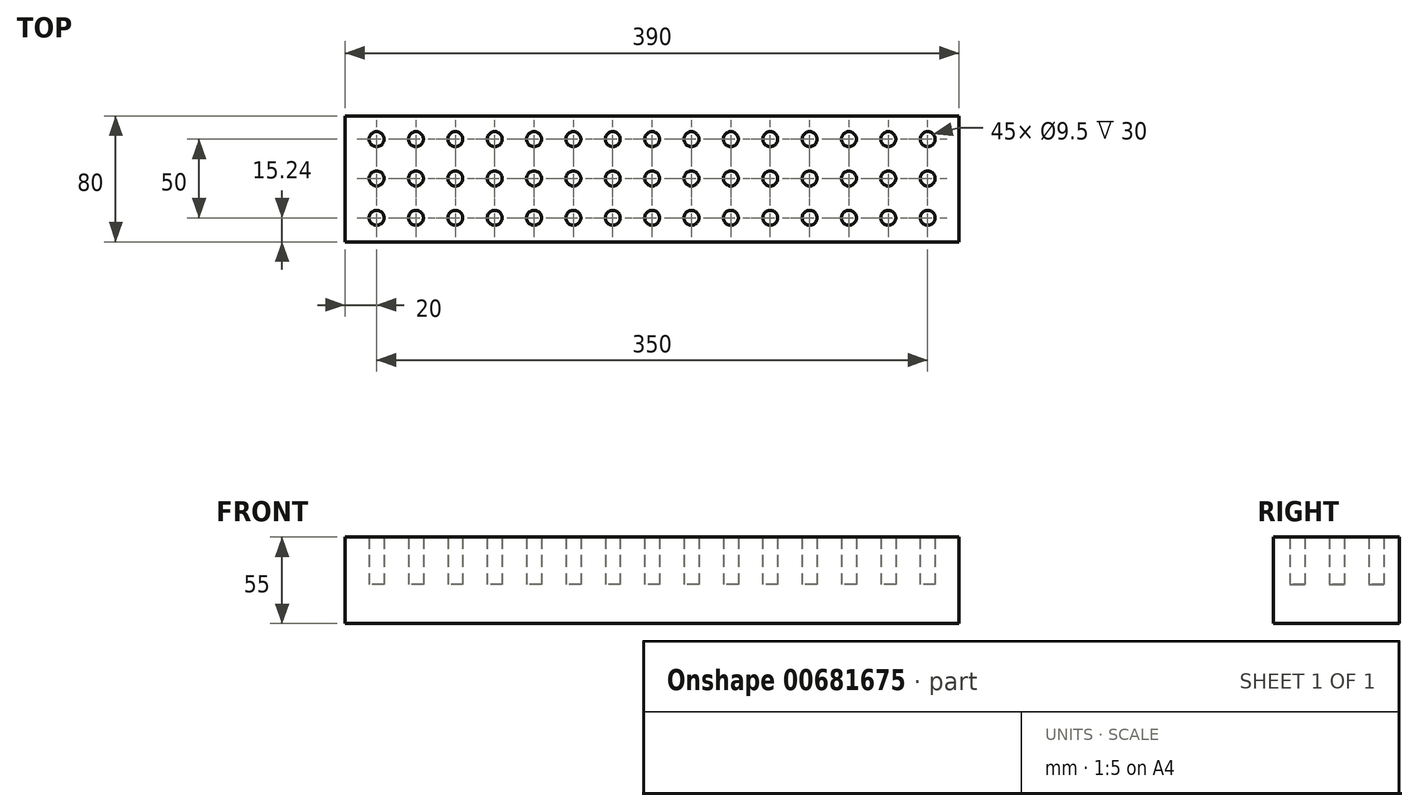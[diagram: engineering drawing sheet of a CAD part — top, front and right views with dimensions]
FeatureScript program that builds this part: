
annotation { "Feature Type Name" : "Feature", "Feature Type Description" : "" }
export const myFeature = defineFeature(function(context is Context, id is Id, definition is map)
    precondition{}
    {
        {
            var Q0;
            Q0=qCreatedBy(makeId("Top.planeOp"),FACE);
            var sketch = newSketch(context, id + "F0", { "sketchPlane" : qUnion([Q0])});
            skCircle(sketch, "E0.cCircle", {"center": v(0, 0) * mm, "radius": 4.11 * mm, "construction": true});
            skLineSegment(sketch, "E0.0", {"start": v(-0.03, 4.75) * mm, "end": v(4.1, 2.4) * mm});
            skLineSegment(sketch, "E0.1", {"start": v(4.1, 2.4) * mm, "end": v(4.13, -2.35) * mm});
            skLineSegment(sketch, "E0.2", {"start": v(4.13, -2.35) * mm, "end": v(0.03, -4.75) * mm});
            skLineSegment(sketch, "E0.3", {"start": v(0.03, -4.75) * mm, "end": v(-4.1, -2.4) * mm});
            skLineSegment(sketch, "E0.4", {"start": v(-4.1, -2.4) * mm, "end": v(-4.13, 2.35) * mm});
            skLineSegment(sketch, "E0.5", {"start": v(-4.13, 2.35) * mm, "end": v(-0.03, 4.75) * mm});
            skPoint(sketch, "E0.0.midPoint", {"position": v(2.04, 3.57) * mm});
            skCircle(sketch, "E1", {"center": v(0, 0) * mm, "radius": 4.75 * mm});
            skCircle(sketch, "E2.0.1.0", {"center": v(0, 25) * mm, "radius": 4.75 * mm});
            skCircle(sketch, "E2.0.2.0", {"center": v(0, 50) * mm, "radius": 4.75 * mm});
            skCircle(sketch, "E2.1.0.0", {"center": v(25, 0) * mm, "radius": 4.75 * mm});
            skCircle(sketch, "E2.1.1.0", {"center": v(25, 25) * mm, "radius": 4.75 * mm});
            skCircle(sketch, "E2.1.2.0", {"center": v(25, 50) * mm, "radius": 4.75 * mm});
            skCircle(sketch, "E2.2.0.0", {"center": v(50, 0) * mm, "radius": 4.75 * mm});
            skCircle(sketch, "E2.2.1.0", {"center": v(50, 25) * mm, "radius": 4.75 * mm});
            skCircle(sketch, "E2.2.2.0", {"center": v(50, 50) * mm, "radius": 4.75 * mm});
            skCircle(sketch, "E2.3.0.0", {"center": v(75, 0) * mm, "radius": 4.75 * mm});
            skCircle(sketch, "E2.3.1.0", {"center": v(75, 25) * mm, "radius": 4.75 * mm});
            skCircle(sketch, "E2.3.2.0", {"center": v(75, 50) * mm, "radius": 4.75 * mm});
            skCircle(sketch, "E2.4.0.0", {"center": v(100, 0) * mm, "radius": 4.75 * mm});
            skCircle(sketch, "E2.4.1.0", {"center": v(100, 25) * mm, "radius": 4.75 * mm});
            skCircle(sketch, "E2.4.2.0", {"center": v(100, 50) * mm, "radius": 4.75 * mm});
            skCircle(sketch, "E2.5.0.0", {"center": v(125, 0) * mm, "radius": 4.75 * mm});
            skCircle(sketch, "E2.5.1.0", {"center": v(125, 25) * mm, "radius": 4.75 * mm});
            skCircle(sketch, "E2.5.2.0", {"center": v(125, 50) * mm, "radius": 4.75 * mm});
            skCircle(sketch, "E2.6.0.0", {"center": v(150, 0) * mm, "radius": 4.75 * mm});
            skCircle(sketch, "E2.6.1.0", {"center": v(150, 25) * mm, "radius": 4.75 * mm});
            skCircle(sketch, "E2.6.2.0", {"center": v(150, 50) * mm, "radius": 4.75 * mm});
            skCircle(sketch, "E2.7.0.0", {"center": v(175, 0) * mm, "radius": 4.75 * mm});
            skCircle(sketch, "E2.7.1.0", {"center": v(175, 25) * mm, "radius": 4.75 * mm});
            skCircle(sketch, "E2.7.2.0", {"center": v(175, 50) * mm, "radius": 4.75 * mm});
            skCircle(sketch, "E2.8.0.0", {"center": v(200, 0) * mm, "radius": 4.75 * mm});
            skCircle(sketch, "E2.8.1.0", {"center": v(200, 25) * mm, "radius": 4.75 * mm});
            skCircle(sketch, "E2.8.2.0", {"center": v(200, 50) * mm, "radius": 4.75 * mm});
            skCircle(sketch, "E2.9.0.0", {"center": v(225, 0) * mm, "radius": 4.75 * mm});
            skCircle(sketch, "E2.9.1.0", {"center": v(225, 25) * mm, "radius": 4.75 * mm});
            skCircle(sketch, "E2.9.2.0", {"center": v(225, 50) * mm, "radius": 4.75 * mm});
            skCircle(sketch, "E2.10.0.0", {"center": v(250, 0) * mm, "radius": 4.75 * mm});
            skCircle(sketch, "E2.10.1.0", {"center": v(250, 25) * mm, "radius": 4.75 * mm});
            skCircle(sketch, "E2.10.2.0", {"center": v(250, 50) * mm, "radius": 4.75 * mm});
            skCircle(sketch, "E2.11.0.0", {"center": v(275, 0) * mm, "radius": 4.75 * mm});
            skCircle(sketch, "E2.11.1.0", {"center": v(275, 25) * mm, "radius": 4.75 * mm});
            skCircle(sketch, "E2.11.2.0", {"center": v(275, 50) * mm, "radius": 4.75 * mm});
            skCircle(sketch, "E2.12.0.0", {"center": v(300, 0) * mm, "radius": 4.75 * mm});
            skCircle(sketch, "E2.12.1.0", {"center": v(300, 25) * mm, "radius": 4.75 * mm});
            skCircle(sketch, "E2.12.2.0", {"center": v(300, 50) * mm, "radius": 4.75 * mm});
            skCircle(sketch, "E2.13.0.0", {"center": v(325, 0) * mm, "radius": 4.75 * mm});
            skCircle(sketch, "E2.13.1.0", {"center": v(325, 25) * mm, "radius": 4.75 * mm});
            skCircle(sketch, "E2.13.2.0", {"center": v(325, 50) * mm, "radius": 4.75 * mm});
            skCircle(sketch, "E2.14.0.0", {"center": v(350, 0) * mm, "radius": 4.75 * mm});
            skCircle(sketch, "E2.14.1.0", {"center": v(350, 25) * mm, "radius": 4.75 * mm});
            skCircle(sketch, "E2.14.2.0", {"center": v(350, 50) * mm, "radius": 4.75 * mm});
            skLineSegment(sketch, "E2.direction1", {"start": v(0, 0) * mm, "end": v(25, 0) * mm, "construction": true});
            skLineSegment(sketch, "E2.direction2", {"start": v(0, 0) * mm, "end": v(0, 25) * mm, "construction": true});
            skLineSegment(sketch, "E3.bottom", {"start": v(-20, -15.24) * mm, "end": v(370, -15.24) * mm});
            skLineSegment(sketch, "E3.top", {"start": v(-20, 64.76) * mm, "end": v(370, 64.76) * mm});
            skLineSegment(sketch, "E3.left", {"start": v(-20, -15.24) * mm, "end": v(-20, 64.76) * mm});
            skLineSegment(sketch, "E3.right", {"start": v(370, -15.24) * mm, "end": v(370, 64.76) * mm});
            skLineSegment(sketch, "E4", {"start": v(175, 64.76) * mm, "end": v(175, 50) * mm, "construction": true});
            skSolve(sketch);
        }
        {
            var Q0;
            Q0=makeQuery(id+"F0.imprint","IMPRINT",FACE,{"disambiguationData":[TD([[makeQuery(id+"F0.imprint","IMPRINT",EDGE,{"derivedFrom":sQuery(id+"F0.wireOp",EDGE,"E2.0.1.0")}),-1.0]])]});
            extrude(context, id + "F1", {"entities" : qUnion([Q0]), "depth" : 30 * mm, "offsetDistance" : 25 * mm});
        }
        {
            var Q0;
            Q0=makeQuery(id+"F1.opExtrude","CAP_FACE",FACE,{"disambiguationData":[OSD([sQuery(id+"F0.wireOp",EDGE,"E1"),sQuery(id+"F0.wireOp",EDGE,"E2.0.1.0"),sQuery(id+"F0.wireOp",EDGE,"E2.0.2.0"),sQuery(id+"F0.wireOp",EDGE,"E2.1.0.0"),sQuery(id+"F0.wireOp",EDGE,"E2.1.1.0"),sQuery(id+"F0.wireOp",EDGE,"E2.1.2.0"),sQuery(id+"F0.wireOp",EDGE,"E2.2.0.0"),sQuery(id+"F0.wireOp",EDGE,"E2.2.1.0"),sQuery(id+"F0.wireOp",EDGE,"E2.2.2.0"),sQuery(id+"F0.wireOp",EDGE,"E2.3.0.0"),sQuery(id+"F0.wireOp",EDGE,"E2.3.1.0"),sQuery(id+"F0.wireOp",EDGE,"E2.3.2.0"),sQuery(id+"F0.wireOp",EDGE,"E2.4.0.0"),sQuery(id+"F0.wireOp",EDGE,"E2.4.1.0"),sQuery(id+"F0.wireOp",EDGE,"E2.4.2.0"),sQuery(id+"F0.wireOp",EDGE,"E2.5.0.0"),sQuery(id+"F0.wireOp",EDGE,"E2.5.1.0"),sQuery(id+"F0.wireOp",EDGE,"E2.5.2.0"),sQuery(id+"F0.wireOp",EDGE,"E2.6.0.0"),sQuery(id+"F0.wireOp",EDGE,"E2.6.1.0"),sQuery(id+"F0.wireOp",EDGE,"E2.6.2.0"),sQuery(id+"F0.wireOp",EDGE,"E2.7.0.0"),sQuery(id+"F0.wireOp",EDGE,"E2.7.1.0"),sQuery(id+"F0.wireOp",EDGE,"E2.7.2.0"),sQuery(id+"F0.wireOp",EDGE,"E2.8.0.0"),sQuery(id+"F0.wireOp",EDGE,"E2.8.1.0"),sQuery(id+"F0.wireOp",EDGE,"E2.8.2.0"),sQuery(id+"F0.wireOp",EDGE,"E2.9.0.0"),sQuery(id+"F0.wireOp",EDGE,"E2.9.1.0"),sQuery(id+"F0.wireOp",EDGE,"E2.9.2.0"),sQuery(id+"F0.wireOp",EDGE,"E2.10.0.0"),sQuery(id+"F0.wireOp",EDGE,"E2.10.1.0"),sQuery(id+"F0.wireOp",EDGE,"E2.10.2.0"),sQuery(id+"F0.wireOp",EDGE,"E2.11.0.0"),sQuery(id+"F0.wireOp",EDGE,"E2.11.1.0"),sQuery(id+"F0.wireOp",EDGE,"E2.11.2.0"),sQuery(id+"F0.wireOp",EDGE,"E2.12.0.0"),sQuery(id+"F0.wireOp",EDGE,"E2.12.1.0"),sQuery(id+"F0.wireOp",EDGE,"E2.12.2.0"),sQuery(id+"F0.wireOp",EDGE,"E2.13.0.0"),sQuery(id+"F0.wireOp",EDGE,"E2.13.1.0"),sQuery(id+"F0.wireOp",EDGE,"E2.13.2.0"),sQuery(id+"F0.wireOp",EDGE,"E2.14.0.0"),sQuery(id+"F0.wireOp",EDGE,"E2.14.1.0"),sQuery(id+"F0.wireOp",EDGE,"E2.14.2.0"),sQuery(id+"F0.wireOp",EDGE,"E3.bottom"),sQuery(id+"F0.wireOp",EDGE,"E3.top"),sQuery(id+"F0.wireOp",EDGE,"E3.left"),sQuery(id+"F0.wireOp",EDGE,"E3.right")])],"isStart":true});
            var sketch = newSketch(context, id + "F2", { "sketchPlane" : qUnion([Q0])});
            skLineSegment(sketch, "E5.bottom", {"start": v(-20, 15.24) * mm, "end": v(370, 15.24) * mm});
            skLineSegment(sketch, "E5.top", {"start": v(-20, -64.76) * mm, "end": v(370, -64.76) * mm});
            skLineSegment(sketch, "E5.left", {"start": v(-20, 15.24) * mm, "end": v(-20, -64.76) * mm});
            skLineSegment(sketch, "E5.right", {"start": v(370, 15.24) * mm, "end": v(370, -64.76) * mm});
            skSolve(sketch);
        }
        {
            var Q0;
            Q0 = qSketchRegion(id + "F2", true);
            extrude(context, id + "F3", {"entities" : qUnion([Q0]), "operationType" : NewBodyOperationType.ADD, "depth" : 25 * mm, "offsetDistance" : 25 * mm});
        }
    });
